# Revit family: 01-70-035-DN200-300
name_source: partatom
category: Pipe Accessories
units: mm (PartAtom-declared; Revit-internal decimal feet)

## family parameters
Always vertical = No
Cut with Voids When Loaded = No
Part Type = Valve - Breaks Into
Round Connector Dimension = Use Diameter
Shared = No
Work Plane-Based = No

## types (5) — shared parameters
Body_Wallthickness = 10 mm  [stored 0.0328084 ft]
Body_Wallthickness_1 = 20 mm  [stored 0.0656168 ft]
Body_Wallthickness_2 = 5 mm  [stored 0.0164042 ft]
DN200_PN16 = 01-200-70-0146499
DN225_PN16 = 01-225-70-0146499
DN250_PN 16 = 01-250-70-016
DN280_PN 16 = 01-280-70-016
DN315_PN16 = 01-315-70-016
Description_ = AVK GATE VALVE, SUPA PLUS™
Fillet_Thickness = 24 mm  [stored 0.0787402 ft]
Ftc = 4 mm  [stored 0.0131234 ft]
Name_Height_reference = 10 mm  [stored 0.0328084 ft]
R2f = 60 mm  [stored 0.19685 ft]
Rib_Thickness = 18 mm  [stored 0.0590551 ft]
Search_table = 01-70-035-DN200-300
URL product pages = https://www.avkvalves.com
zero-valued in all types: Bottom_Reference

## per-type parameters (varying)
- DN200_PN16: At=147 mm; Body_Height=220 mm; Body_depth=294 mm; Body_width=108 mm; Bonnet_Flange_Depth=332 mm; Bonnet_Flange_Width=132 mm; Bonnet_Flange_cut=13 mm; Bonnet_Flange_thickness=25 mm  [stored 0.082021 ft]; Bonnet_Height=85 mm  [stored 0.278871 ft]; Bonnet_Reference_height=210 mm; Bonnet_Thickness=110 mm; Bt=110 mm; Bt_2=102 mm; CL _Thickness=34 mm  [stored 0.111549 ft]; CL_Height=152 mm; Cut_Reference=852 mm; D=63 mm  [stored 0.206693 ft]; D1=10 mm  [stored 0.0328084 ft]; D2=34 mm  [stored 0.111549 ft]; Dd=200 mm; Dd_ref=120 mm; Dd_ref_1=100 mm; E=15 mm  [stored 0.0492126 ft]; F=12 mm  [stored 0.0393701 ft]; F1=27 mm  [stored 0.0885827 ft]; Flange_OR=170 mm; Flange_Thickness=20 mm  [stored 0.0656168 ft]; Flange_Thickness_cut=35 mm  [stored 0.114829 ft]; Flange_depth=332 mm; Flange_width=41 mm; Ftc_reference_height=170 mm; H=495 mm; H1=461 mm; H2=158 mm; H3=653 mm; Horizontal_Flange_width=316 mm; ID (Radius)=100 mm; L=426 mm; L1=249 mm; L2=120 mm; L_Dia=200 mm; L_ref=338 mm; Name_Reference=183 mm; Name_Width=54 mm  [stored 0.177165 ft]; Neck_H=89 mm  [stored 0.291995 ft]; Neck_T=32 mm  [stored 0.104987 ft]; Neck_T2=30 mm  [stored 0.0984252 ft]; Nominal Diameter (DN)=200 mm; OD=113 mm; R1tv=1700 mm; RF_Dia=133 mm; Rf=527 mm; Rib_Height_Reference_1=120 mm; Rib_Height_Reference_2=110 mm; Rib_Height_Reference_3=100 mm; Rib_Height_Reference_4=180 mm; Rib_Width_1=54 mm  [stored 0.177165 ft]; Rib_Width_2=54 mm  [stored 0.177165 ft]; Rib_Width_3=54 mm  [stored 0.177165 ft]; Rib_depth_1=54 mm  [stored 0.177165 ft]; Rib_depth_2=54 mm  [stored 0.177165 ft]; Rib_depth_3=54 mm  [stored 0.177165 ft]; Rt=567 mm
- DN225_PN16: At=147 mm; Body_Height=220 mm; Body_depth=294 mm; Body_width=108 mm; Bonnet_Flange_Depth=332 mm; Bonnet_Flange_Width=132 mm; Bonnet_Flange_cut=13 mm; Bonnet_Flange_thickness=25 mm  [stored 0.082021 ft]; Bonnet_Height=85 mm  [stored 0.278871 ft]; Bonnet_Reference_height=210 mm; Bonnet_Thickness=110 mm; Bt=110 mm; Bt_2=102 mm; CL _Thickness=34 mm  [stored 0.111549 ft]; CL_Height=152 mm; Cut_Reference=966 mm; D=63 mm  [stored 0.206693 ft]; D1=10 mm  [stored 0.0328084 ft]; D2=47 mm  [stored 0.154199 ft]; Dd=225 mm; Dd_ref=133 mm; Dd_ref_1=113 mm; E=15 mm  [stored 0.0492126 ft]; F=12 mm  [stored 0.0393701 ft]; F1=27 mm  [stored 0.0885827 ft]; Flange_OR=170 mm; Flange_Thickness=20 mm  [stored 0.0656168 ft]; Flange_Thickness_cut=35 mm  [stored 0.114829 ft]; Flange_depth=332 mm; Flange_width=39 mm  [stored 0.127953 ft]; Ftc_reference_height=170 mm; H=495 mm; H1=448 mm; H2=165 mm; H3=660 mm; Horizontal_Flange_width=330 mm; ID (Radius)=100 mm; L=483 mm; L1=249 mm; L2=110 mm; L_Dia=200 mm; L_ref=366 mm; Name_Reference=183 mm; Name_Width=54 mm  [stored 0.177165 ft]; Neck_H=76 mm; Neck_T=32 mm  [stored 0.104987 ft]; Neck_T2=30 mm  [stored 0.0984252 ft]; Nominal Diameter (DN)=200 mm; OD=127 mm; R1tv=1700 mm; RF_Dia=133 mm; Rf=550 mm; Rib_Height_Reference_1=120 mm; Rib_Height_Reference_2=110 mm; Rib_Height_Reference_3=100 mm; Rib_Height_Reference_4=180 mm; Rib_Width_1=54 mm  [stored 0.177165 ft]; Rib_Width_2=54 mm  [stored 0.177165 ft]; Rib_Width_3=54 mm  [stored 0.177165 ft]; Rib_depth_1=54 mm  [stored 0.177165 ft]; Rib_depth_2=54 mm  [stored 0.177165 ft]; Rib_depth_3=54 mm  [stored 0.177165 ft]; Rt=567 mm
- DN250_PN 16: At=171 mm; Body_Height=340 mm; Body_depth=342 mm; Body_width=124 mm; Bonnet_Flange_Depth=372 mm; Bonnet_Flange_Width=158 mm; Bonnet_Flange_cut=13 mm; Bonnet_Flange_thickness=25 mm  [stored 0.082021 ft]; Bonnet_Height=100 mm; Bonnet_Reference_height=330 mm; Bonnet_Thickness=126 mm; Bt=126 mm; Bt_2=118 mm; CL _Thickness=42 mm  [stored 0.137795 ft]; CL_Height=176 mm; Cut_Reference=1058 mm; D=88 mm  [stored 0.288714 ft]; D1=15 mm  [stored 0.0492126 ft]; D2=47 mm  [stored 0.154199 ft]; Dd=250 mm; Dd_ref=145 mm; Dd_ref_1=125 mm; E=13 mm; F=14 mm  [stored 0.0459318 ft]; F1=31 mm  [stored 0.101706 ft]; Flange_OR=200 mm; Flange_Thickness=22 mm  [stored 0.0721785 ft]; Flange_Thickness_cut=38 mm  [stored 0.124672 ft]; Flange_depth=372 mm; Flange_width=39 mm  [stored 0.127953 ft]; Ftc_reference_height=200 mm; H=664 mm; H1=617 mm; H2=174 mm; H3=838 mm; Horizontal_Flange_width=348 mm; ID (Radius)=125 mm; L=529 mm; L1=354 mm; L2=143 mm; L_Dia=250 mm; L_ref=442 mm; Name_Reference=270 mm; Name_Width=62 mm  [stored 0.203412 ft]; Neck_H=101 mm; Neck_T=40 mm  [stored 0.131234 ft]; Neck_T2=38 mm  [stored 0.124672 ft]; Nominal Diameter (DN)=250 mm; OD=72 mm  [stored 0.23622 ft]; R1tv=2000 mm; RF_Dia=160 mm; Rf=580 mm; Rib_Height_Reference_1=90 mm  [stored 0.295276 ft]; Rib_Height_Reference_2=110 mm; Rib_Height_Reference_3=100 mm; Rib_Height_Reference_4=200 mm; Rib_Width_1=145 mm; Rib_Width_2=145 mm; Rib_Width_3=62 mm  [stored 0.203412 ft]; Rib_depth_1=372 mm; Rib_depth_2=62 mm  [stored 0.203412 ft]; Rib_depth_3=62 mm  [stored 0.203412 ft]; Rt=667 mm
- DN280_PN 16: At=171 mm; Body_Height=340 mm; Body_depth=342 mm; Body_width=124 mm; Bonnet_Flange_Depth=372 mm; Bonnet_Flange_Width=158 mm; Bonnet_Flange_cut=13 mm; Bonnet_Flange_thickness=25 mm  [stored 0.082021 ft]; Bonnet_Height=100 mm; Bonnet_Reference_height=330 mm; Bonnet_Thickness=126 mm; Bt=126 mm; Bt_2=118 mm; CL _Thickness=42 mm  [stored 0.137795 ft]; CL_Height=176 mm; Cut_Reference=1058 mm; D=88 mm  [stored 0.288714 ft]; D1=15 mm  [stored 0.0492126 ft]; D2=47 mm  [stored 0.154199 ft]; Dd=280 mm; Dd_ref=160 mm; Dd_ref_1=140 mm; E=13 mm; F=14 mm  [stored 0.0459318 ft]; F1=31 mm  [stored 0.101706 ft]; Flange_OR=200 mm; Flange_Thickness=22 mm  [stored 0.0721785 ft]; Flange_Thickness_cut=37 mm; Flange_depth=372 mm; Flange_width=39 mm  [stored 0.127953 ft]; Ftc_reference_height=200 mm; H=664 mm; H1=617 mm; H2=184 mm; H3=848 mm; Horizontal_Flange_width=368 mm; ID (Radius)=125 mm; L=529 mm; L1=354 mm; L2=155 mm; L_Dia=250 mm; L_ref=442 mm; Name_Reference=270 mm; Name_Width=62 mm  [stored 0.203412 ft]; Neck_H=101 mm; Neck_T=40 mm  [stored 0.131234 ft]; Neck_T2=38 mm  [stored 0.124672 ft]; Nominal Diameter (DN)=250 mm; OD=79 mm; R1tv=2000 mm; RF_Dia=160 mm; Rf=613 mm; Rib_Height_Reference_1=90 mm  [stored 0.295276 ft]; Rib_Height_Reference_2=110 mm; Rib_Height_Reference_3=100 mm; Rib_Height_Reference_4=200 mm; Rib_Width_1=140 mm; Rib_Width_2=140 mm; Rib_Width_3=62 mm  [stored 0.203412 ft]; Rib_depth_1=372 mm; Rib_depth_2=62 mm  [stored 0.203412 ft]; Rib_depth_3=62 mm  [stored 0.203412 ft]; Rt=667 mm
- DN315_PN16: At=209 mm; Body_Height=370 mm; Body_depth=418 mm; Body_width=157 mm; Bonnet_Flange_Depth=432 mm; Bonnet_Flange_Width=206 mm; Bonnet_Flange_cut=18 mm  [stored 0.0590551 ft]; Bonnet_Flange_thickness=35 mm  [stored 0.114829 ft]; Bonnet_Height=114 mm; Bonnet_Reference_height=360 mm; Bonnet_Thickness=160 mm; Bt=160 mm; Bt_2=151 mm; CL _Thickness=59 mm; CL_Height=214 mm; Cut_Reference=1140 mm; D=88 mm  [stored 0.288714 ft]; D1=15 mm  [stored 0.0492126 ft]; D2=47 mm  [stored 0.154199 ft]; Dd=315 mm; Dd_ref=178 mm; Dd_ref_1=158 mm; E=13 mm; F=14 mm  [stored 0.0459318 ft]; F1=31 mm  [stored 0.101706 ft]; Flange_OR=228 mm; Flange_Thickness=25 mm  [stored 0.082021 ft]; Flange_Thickness_cut=39 mm  [stored 0.127953 ft]; Flange_depth=432 mm; Flange_width=39 mm  [stored 0.127953 ft]; Ftc_reference_height=228 mm; H=740 mm; H1=693 mm; H2=208 mm; H3=948 mm; Horizontal_Flange_width=416 mm; ID (Radius)=150 mm; L=570 mm; L1=354 mm; L2=184 mm; L_Dia=300 mm; L_ref=462 mm; Name_Reference=250 mm; Name_Width=79 mm; Neck_H=109 mm; Neck_T=57 mm; Neck_T2=55 mm  [stored 0.180446 ft]; Nominal Diameter (DN)=300 mm; OD=90 mm  [stored 0.295276 ft]; R1tv=2280 mm; RF_Dia=185 mm; Rf=693 mm; Rib_Height_Reference_1=178 mm; Rib_Height_Reference_2=285 mm; Rib_Height_Reference_3=170 mm; Rib_Height_Reference_4=300 mm; Rib_Width_1=185 mm; Rib_Width_2=185 mm; Rib_Width_3=79 mm; Rib_depth_1=432 mm; Rib_depth_2=432 mm; Rib_depth_3=79 mm; Rt=760 mm

note: [stored X ft] marks values corroborated as IEEE doubles in the binary element streams (Revit-internal decimal feet)

## geometry (parser evidence)
native form markers: Sweep x2
no freeform markers — native parametric forms only
